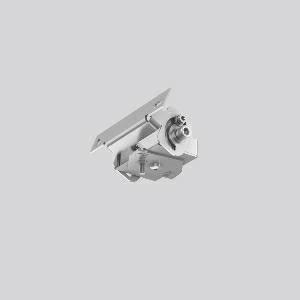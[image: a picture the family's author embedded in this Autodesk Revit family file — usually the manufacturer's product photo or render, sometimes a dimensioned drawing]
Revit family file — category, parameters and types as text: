
# Revit family: linedo_decke_wand_ausleger_982812_000_5280
name_source: partatom
category: Lighting Fixtures
units: mm (PartAtom-declared; Revit-internal decimal feet)

## family parameters
Cut with Voids When Loaded = No
Host = Face
Light Source = No
Part Type = Normal
Room Calculation Point = No
Round Connector Dimension = Use Diameter
Shared = No

## types (1)
- LINEDO Decke Wand Ausleger
    Apparent Load = 0 VA
    Default Elevation = 1800 mm
    Description = Ceiling/wall extension made of stainless steel. For 180°-pivotable horizontal installation of LINEDO luminaire modules, movable. 2 ceiling and wall brackets are required per luminaire module. With this accessory, the protection type of the luminaire module can be reduced to IP 20.
Colour: stainless steel
Length: 103 mm
Width: 47 mm
Height: 45 mm
Weight: 154 g
Type of Installation: Wall (surface)
    Height = 45 mm
    Lamp = 0 x
    Length = 103 mm
    Luminous efficacy = 0 lm/W
    Manufacturer = RZB
    ModVariant = No
    Model = 982812.000
    Mounting Place = Ceiling
    Mounting Type = Surface mounted
    Number of Poles = 1
    OnlyDefault = Yes
    Power Factor = 1
    Product Name = LINEDO Decke Wand Ausleger
    Product group = Surface mounted continuous line luminaire system
    ProductGroupID = 310
    Protection Class = Protection class
    Protection Degree = Degree of protection
    RLX_Detail_Level = 1
    RLX_Emergency_Light_Flux = 0 lm
    RLX_Emergency_Type = 0
    RLX_Emergency_Type_DB = No
    RlxData = <blob elided: 12625 chars, md5=2a422f66>
    Standby Power = 0 W
    System Light Flux = 0 lm
    System Power = 0 W
    Type Comments = Product without accessories
    Type Image = 982812.000.jpg
    URL = http://relux.com
    VarID = ---
    Voltage = 0 V
    Weight = 0.00 kg
    Width = 47 mm

## geometry (parser evidence)
native form markers: Sweep x8
no freeform markers — native parametric forms only
